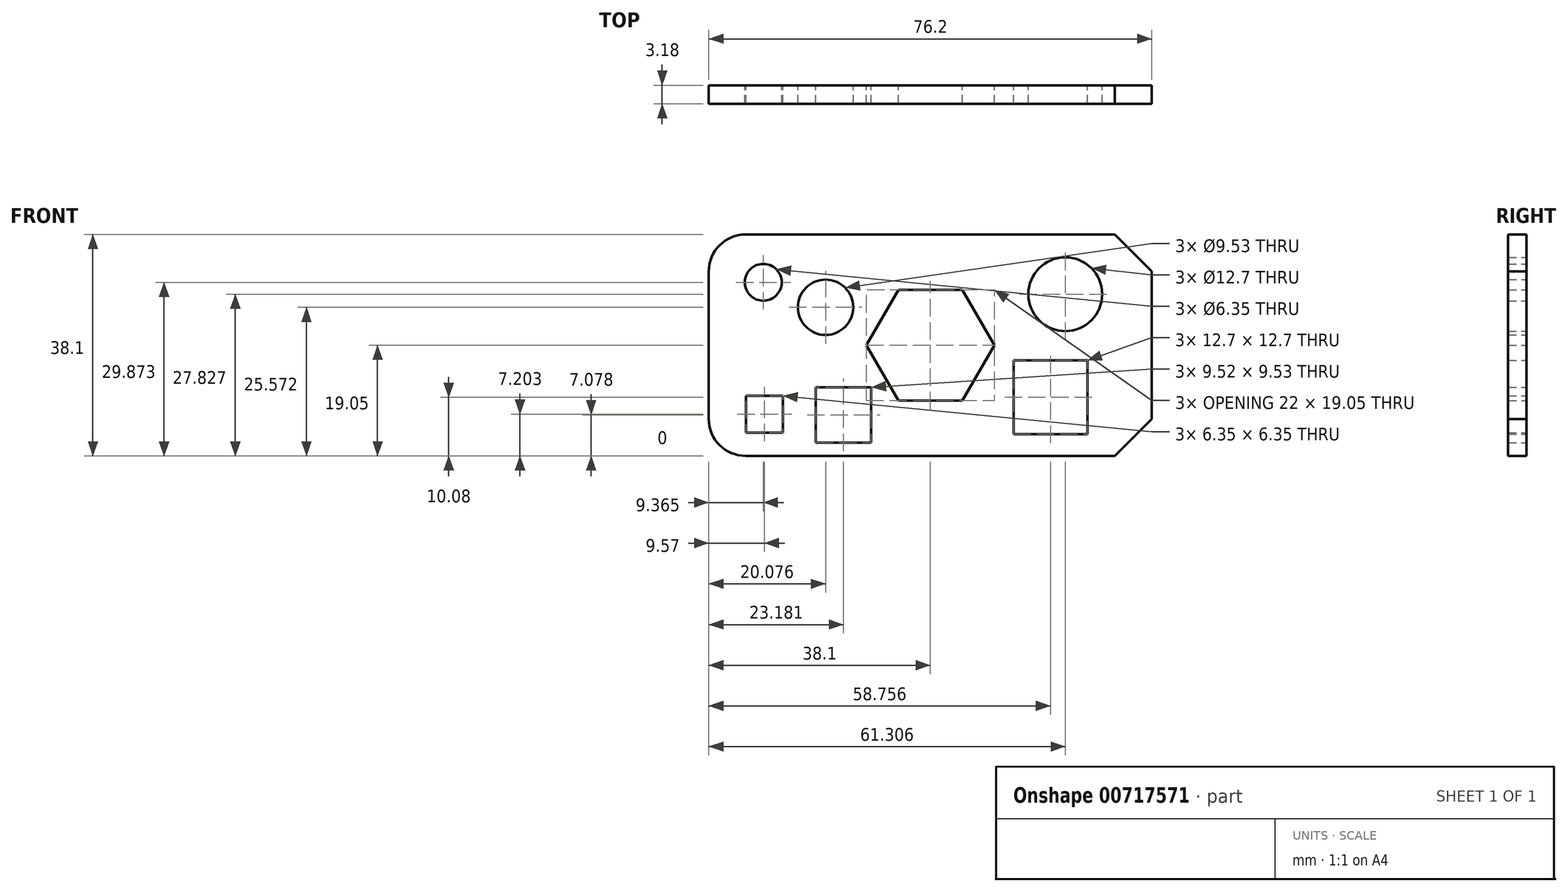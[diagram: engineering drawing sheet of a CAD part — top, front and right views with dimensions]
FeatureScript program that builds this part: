
annotation { "Feature Type Name" : "Feature", "Feature Type Description" : "" }
export const myFeature = defineFeature(function(context is Context, id is Id, definition is map)
    precondition{}
    {
        {
            var Q0;
            Q0=qCreatedBy(makeId("Front.planeOp"),FACE);
            var sketch = newSketch(context, id + "F0", { "sketchPlane" : qUnion([Q0])});
            skLineSegment(sketch, "E0.bottom", {"start": v(38.1, 19.05) * mm, "end": v(-38.1, 19.05) * mm});
            skLineSegment(sketch, "E0.top", {"start": v(38.1, -19.05) * mm, "end": v(-38.1, -19.05) * mm});
            skLineSegment(sketch, "E0.left", {"start": v(38.1, 19.05) * mm, "end": v(38.1, -19.05) * mm});
            skLineSegment(sketch, "E0.right", {"start": v(-38.1, 19.05) * mm, "end": v(-38.1, -19.05) * mm});
            skCircle(sketch, "E1", {"center": v(-28.73, 10.82) * mm, "radius": 3.18 * mm});
            skCircle(sketch, "E2", {"center": v(23.2, 8.78) * mm, "radius": 6.35 * mm});
            skLineSegment(sketch, "E3.bottom", {"start": v(-25.36, -8.67) * mm, "end": v(-31.7, -8.67) * mm});
            skLineSegment(sketch, "E3.top", {"start": v(-25.36, -15.02) * mm, "end": v(-31.7, -15.02) * mm});
            skLineSegment(sketch, "E3.left", {"start": v(-25.36, -8.67) * mm, "end": v(-25.36, -15.02) * mm});
            skLineSegment(sketch, "E3.right", {"start": v(-31.7, -8.67) * mm, "end": v(-31.7, -15.02) * mm});
            skPoint(sketch, "E3.middle", {"position": v(-28.53, -11.85) * mm});
            skLineSegment(sketch, "E4.bottom", {"start": v(14.3, -2.62) * mm, "end": v(27, -2.62) * mm});
            skLineSegment(sketch, "E4.top", {"start": v(14.3, -15.32) * mm, "end": v(27, -15.32) * mm});
            skLineSegment(sketch, "E4.left", {"start": v(14.3, -2.62) * mm, "end": v(14.3, -15.32) * mm});
            skLineSegment(sketch, "E4.right", {"start": v(27, -2.62) * mm, "end": v(27, -15.32) * mm});
            skPoint(sketch, "E4.middle", {"position": v(20.66, -8.97) * mm});
            skCircle(sketch, "E5.cCircle", {"center": v(0, 0) * mm, "radius": 9.53 * mm, "construction": true});
            skLineSegment(sketch, "E5.0", {"start": v(-5.5, 9.53) * mm, "end": v(5.5, 9.53) * mm});
            skLineSegment(sketch, "E5.1", {"start": v(5.5, 9.53) * mm, "end": v(11, 0) * mm});
            skLineSegment(sketch, "E5.2", {"start": v(11, 0) * mm, "end": v(5.5, -9.53) * mm});
            skLineSegment(sketch, "E5.3", {"start": v(5.5, -9.52) * mm, "end": v(-5.5, -9.53) * mm});
            skLineSegment(sketch, "E5.4", {"start": v(-5.5, -9.53) * mm, "end": v(-11, 0) * mm});
            skLineSegment(sketch, "E5.5", {"start": v(-11, 0) * mm, "end": v(-5.5, 9.53) * mm});
            skPoint(sketch, "E5.0.midPoint", {"position": v(0, 9.53) * mm});
            skCircle(sketch, "E6", {"center": v(-18.02, 6.52) * mm, "radius": 4.76 * mm});
            skLineSegment(sketch, "E7.bottom", {"start": v(-10.16, -7.2) * mm, "end": v(-19.68, -7.2) * mm});
            skLineSegment(sketch, "E7.top", {"start": v(-10.16, -16.73) * mm, "end": v(-19.68, -16.73) * mm});
            skLineSegment(sketch, "E7.left", {"start": v(-10.16, -7.2) * mm, "end": v(-10.16, -16.73) * mm});
            skLineSegment(sketch, "E7.right", {"start": v(-19.68, -7.2) * mm, "end": v(-19.68, -16.73) * mm});
            skPoint(sketch, "E7.middle", {"position": v(-14.92, -11.97) * mm});
            skSolve(sketch);
        }
        {
            var Q0;
            Q0=makeQuery(id+"F0.imprint","IMPRINT",FACE,{"disambiguationData":[TD([[makeQuery(id+"F0.imprint","IMPRINT",EDGE,{"derivedFrom":sQuery(id+"F0.wireOp",EDGE,"E0.bottom")}),1.0]])]});
            extrude(context, id + "F1", {"entities" : qUnion([Q0]), "endBound" : BoundingType.SYMMETRIC, "depth" : 3.17 * mm, "offsetDistance" : 25.4 * mm});
        }
        {
            var Q0;
            Q0=makeQuery(id+"F1.opExtrude","SWEPT_EDGE",EDGE,{"disambiguationData":[OSD([sQuery(id+"F0.wireOp",EDGE,"E0.bottom"),sQuery(id+"F0.wireOp",EDGE,"E0.right")])]});
            var Q1;
            Q1=makeQuery(id+"F1.opExtrude","SWEPT_EDGE",EDGE,{"disambiguationData":[OSD([sQuery(id+"F0.wireOp",EDGE,"E0.top"),sQuery(id+"F0.wireOp",EDGE,"E0.right")])]});
            fillet(context, id + "F2", {"entities" : qUnion([Q0, Q1]), "radius" : 6.35 * mm, "tangentPropagation" : true, "allowEdgeOverflow" : false});
        }
        {
            var Q0;
            Q0=makeQuery(id+"F1.opExtrude","SWEPT_EDGE",EDGE,{"disambiguationData":[OSD([sQuery(id+"F0.wireOp",EDGE,"E0.bottom"),sQuery(id+"F0.wireOp",EDGE,"E0.left")])]});
            var Q1;
            Q1=makeQuery(id+"F1.opExtrude","SWEPT_EDGE",EDGE,{"disambiguationData":[OSD([sQuery(id+"F0.wireOp",EDGE,"E0.top"),sQuery(id+"F0.wireOp",EDGE,"E0.left")])]});
            chamfer(context, id + "F3", {"entities" : qUnion([Q0, Q1]), "width" : 6.35 * mm, "tangentPropagation" : true});
        }
    });
